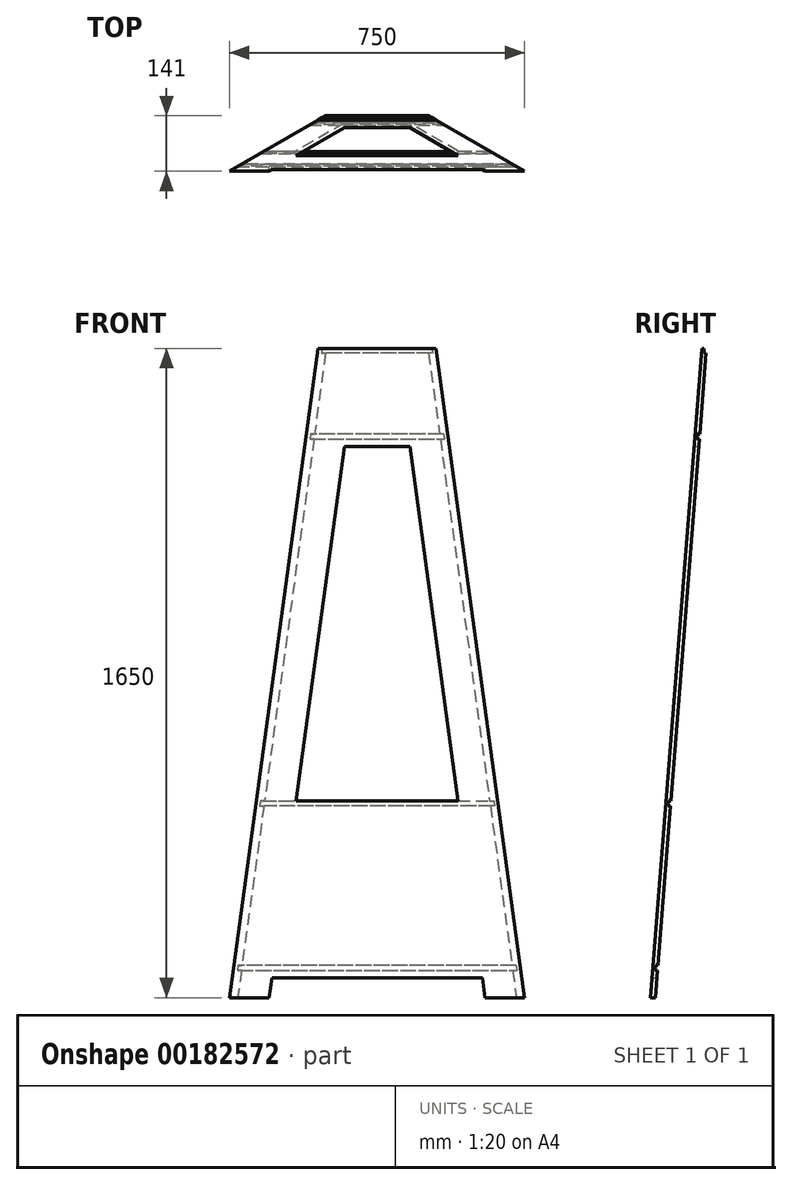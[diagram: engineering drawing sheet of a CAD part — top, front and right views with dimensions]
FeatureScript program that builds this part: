
annotation { "Feature Type Name" : "Feature", "Feature Type Description" : "" }
export const myFeature = defineFeature(function(context is Context, id is Id, definition is map)
    precondition{}
    {
        {
            var Q0;
            Q0=qCreatedBy(makeId("Front.planeOp"),FACE);
            var sketch = newSketch(context, id + "F0", { "sketchPlane" : qUnion([Q0])});
            skLineSegment(sketch, "E0", {"start": v(-375, 0) * mm, "end": v(375, 0) * mm});
            skLineSegment(sketch, "E1", {"start": v(0, 0) * mm, "end": v(0, 1650) * mm});
            skLineSegment(sketch, "E2", {"start": v(-150, 1650) * mm, "end": v(150, 1650) * mm});
            skSolve(sketch);
        }
        {
            var Q0;
            Q0=sQuery(id+"F0.wireOp",EDGE,"E2");
            cPoint(context, id + "F1", {"entities" : qUnion([Q0]), "parameter" : 0.5});
        }
        {
            var Q0;
            Q0=qCreatedBy(id+"F1",VERTEX);
            var Q1;
            Q1=sQuery(id+"F0.wireOp",EDGE,"E1");
            cPlane(context, id + "F2", {"entities" : qUnion([Q0, Q1]), "cplaneType" : CPlaneType.LINE_POINT, "offset" : 25 * mm, "width" : 150 * mm, "height" : 150 * mm});
        }
        {
            var Q0;
            Q0=qCreatedBy(makeId("Top.planeOp"),FACE);
            var sketch = newSketch(context, id + "F3", { "sketchPlane" : qUnion([Q0])});
            skCircle(sketch, "E3.cCircle", {"center": v(0, 0) * mm, "radius": 216.5 * mm, "construction": true});
            skLineSegment(sketch, "E3.0", {"start": v(375, -216.5) * mm, "end": v(-375, -216.5) * mm});
            skLineSegment(sketch, "E3.1", {"start": v(-375, -216.5) * mm, "end": v(0, 433.01) * mm});
            skLineSegment(sketch, "E3.2", {"start": v(0, 433.01) * mm, "end": v(375, -216.5) * mm});
            skPoint(sketch, "E3.0.midPoint", {"position": v(0, -216.5) * mm});
            skSolve(sketch);
        }
        {
            var Q0;
            Q0=qCreatedBy(id+"F2.planeOp",FACE);
            var sketch = newSketch(context, id + "F4", { "sketchPlane" : qUnion([Q0])});
            skCircle(sketch, "E4.cCircle", {"center": v(0, 0) * mm, "radius": 86.6 * mm, "construction": true});
            skLineSegment(sketch, "E4.0", {"start": v(150, -86.6) * mm, "end": v(-150, -86.6) * mm});
            skLineSegment(sketch, "E4.1", {"start": v(-150, -86.6) * mm, "end": v(0, 173.2) * mm});
            skLineSegment(sketch, "E4.2", {"start": v(0, 173.2) * mm, "end": v(150, -86.6) * mm});
            skPoint(sketch, "E4.0.midPoint", {"position": v(0, -86.6) * mm});
            skSolve(sketch);
        }
        {
            var Q0;
            Q0=makeQuery(id+"F3.imprint","IMPRINT",FACE,{"disambiguationData":[TD([[makeQuery(id+"F3.imprint","IMPRINT",EDGE,{"derivedFrom":sQuery(id+"F3.wireOp",EDGE,"E3.0")}),-1.0]])]});
            var Q1;
            Q1=makeQuery(id+"F4.imprint","IMPRINT",FACE,{"disambiguationData":[TD([[makeQuery(id+"F4.imprint","IMPRINT",EDGE,{"derivedFrom":sQuery(id+"F4.wireOp",EDGE,"E4.0")}),-1.0]])]});
            loft(context, id + "F5", {"sheetProfilesArray" : [{ "sheetProfileEntities" : qUnion([Q0]) }, { "sheetProfileEntities" : qUnion([Q1]) }]});
        }
        {
            var Q0;
            {var subQ0=sQuery(id+"F4.wireOp",EDGE,"E4.0");var subQ1=sQuery(id+"F4.wireOp",EDGE,"E4.1");var subQ2=sQuery(id+"F4.wireOp",EDGE,"E4.2");var subQ3=sQuery(id+"F3.wireOp",EDGE,"E3.0");var subQ4=sQuery(id+"F3.wireOp",EDGE,"E3.1");var subQ5=sQuery(id+"F3.wireOp",EDGE,"E3.2");Q0=makeQuery(id+"F5.opLoft","SWEPT_FACE",FACE,{"disambiguationData":[OSD([subQ3,subQ4,subQ5,subQ0,subQ1,subQ2]),TDD([makeQuery(id+"F3.imprint","INTERSECT",VERTEX,{"derivedFrom":[subQ3,subQ5]}),makeQuery(id+"F3.imprint","INTERSECT",VERTEX,{"derivedFrom":[subQ3,subQ4]}),makeQuery(id+"F3.imprint","IMPRINT",EDGE,{"derivedFrom":subQ3}),makeQuery(id+"F4.imprint","INTERSECT",VERTEX,{"derivedFrom":[subQ0,subQ2]}),makeQuery(id+"F4.imprint","INTERSECT",VERTEX,{"derivedFrom":[subQ0,subQ1]}),makeQuery(id+"F4.imprint","IMPRINT",EDGE,{"derivedFrom":subQ0})])]});}
            cPlane(context, id + "F6", {"entities" : qUnion([Q0]), "cplaneType" : CPlaneType.OFFSET, "offset" : 12 * mm, "oppositeDirection" : true, "width" : 150 * mm, "height" : 150 * mm});
        }
        {
            var Q0;
            Q0=qCreatedBy(id+"F6.planeOp",FACE);
            var sketch = newSketch(context, id + "F7", { "sketchPlane" : qUnion([Q0])});
            skCircle(sketch, "E5", {"center": v(0, 812.97) * mm, "radius": 960.24 * mm});
            skSolve(sketch);
        }
        {
            var Q0;
            Q0=qSketchRegion(id+"F7",true);
            extrude(context, id + "F8", {"entities" : qUnion([Q0]), "operationType" : NewBodyOperationType.REMOVE, "endBound" : BoundingType.THROUGH_ALL, "oppositeDirection" : true, "depth" : 25 * mm});
        }
        {
            var Q0;
            Q0=makeQuery(id+"F5.opLoft","CAP_FACE",FACE,{"disambiguationData":[OSD([makeQuery(id+"F4.imprint","IMPRINT",FACE,{"disambiguationData":[TD([[makeQuery(id+"F4.imprint","IMPRINT",EDGE,{"derivedFrom":sQuery(id+"F4.wireOp",EDGE,"E4.0")}),-1.0]])]})])],"isStart":true});
            var sketch = newSketch(context, id + "F9", { "sketchPlane" : qUnion([Q0])});
            skLineSegment(sketch, "E6", {"start": v(150, -86.6) * mm, "end": v(129.15, -74.57) * mm});
            skLineSegment(sketch, "E7", {"start": v(-150, -86.6) * mm, "end": v(-129.15, -74.57) * mm});
            skLineSegment(sketch, "E8", {"start": v(129.15, -74.57) * mm, "end": v(70, -40.41) * mm, "construction": true});
            skLineSegment(sketch, "E9", {"start": v(129.15, -74.57) * mm, "end": v(104.15, -31.26) * mm, "construction": true});
            skLineSegment(sketch, "E10", {"start": v(104.15, -31.26) * mm, "end": v(70, -40.41) * mm, "construction": true});
            skLineSegment(sketch, "E11.MirrorCS", {"start": v(79.15, -74.57) * mm, "end": v(70, -40.41) * mm, "construction": true});
            skLineSegment(sketch, "E12.MirrorCS", {"start": v(129.15, -74.57) * mm, "end": v(79.15, -74.57) * mm, "construction": true});
            skSolve(sketch);
        }
        {
            var Q0;
            Q0=makeQuery(id+"F5.opLoft","SWEPT_EDGE",EDGE,{"disambiguationData":[OSD([sQuery(id+"F3.wireOp",EDGE,"E3.0"),sQuery(id+"F3.wireOp",EDGE,"E3.1"),sQuery(id+"F4.wireOp",EDGE,"E4.0"),sQuery(id+"F4.wireOp",EDGE,"E4.1")])]});
            var Q1;
            Q1=sQuery(id+"F9.wireOp",EDGE,"E7");
            cPlane(context, id + "F10", {"entities" : qUnion([Q0, Q1]), "cplaneType" : CPlaneType.LINE_ANGLE, "offset" : 25 * mm, "angle" : 0 * degree, "width" : 150 * mm, "height" : 150 * mm});
        }
        {
            var Q0;
            Q0=makeQuery(id+"F5.opLoft","SWEPT_EDGE",EDGE,{"disambiguationData":[OSD([sQuery(id+"F3.wireOp",EDGE,"E3.0"),sQuery(id+"F3.wireOp",EDGE,"E3.2"),sQuery(id+"F4.wireOp",EDGE,"E4.0"),sQuery(id+"F4.wireOp",EDGE,"E4.2")])]});
            var Q1;
            Q1=sQuery(id+"F9.wireOp",EDGE,"E6");
            cPlane(context, id + "F11", {"entities" : qUnion([Q0, Q1]), "cplaneType" : CPlaneType.LINE_ANGLE, "offset" : 25 * mm, "angle" : 0 * degree, "width" : 150 * mm, "height" : 150 * mm});
        }
        {
            var Q0;
            Q0=qCreatedBy(id+"F11.planeOp",FACE);
            var sketch = newSketch(context, id + "F12", { "sketchPlane" : qUnion([Q0])});
            skCircle(sketch, "E13", {"center": v(304.07, 817.21) * mm, "radius": 870.23 * mm});
            skSolve(sketch);
        }
        {
            var Q0;
            Q0=qSketchRegion(id+"F12",true);
            extrude(context, id + "F13", {"entities" : qUnion([Q0]), "operationType" : NewBodyOperationType.REMOVE, "oppositeDirection" : true, "depth" : 25 * mm});
        }
        {
            var Q0;
            Q0=qCreatedBy(id+"F10.planeOp",FACE);
            var sketch = newSketch(context, id + "F14", { "sketchPlane" : qUnion([Q0])});
            skCircle(sketch, "E14", {"center": v(291.65, 811.12) * mm, "radius": 892.94 * mm});
            skSolve(sketch);
        }
        {
            var Q0;
            Q0=qSketchRegion(id+"F14",true);
            extrude(context, id + "F15", {"entities" : qUnion([Q0]), "operationType" : NewBodyOperationType.REMOVE, "depth" : 25 * mm});
        }
        {
            var Q0;
            Q0=qCreatedBy(makeId("Front.planeOp"),FACE);
            var sketch = newSketch(context, id + "F16", { "sketchPlane" : qUnion([Q0])});
            skLineSegment(sketch, "E15.0.0", {"start": v(-354.15, 0) * mm, "end": v(-129.15, 1650) * mm, "construction": true});
            skLineSegment(sketch, "E15.0.1", {"start": v(-129.15, 1650) * mm, "end": v(129.15, 1650) * mm});
            skLineSegment(sketch, "E15.0.2", {"start": v(129.15, 1650) * mm, "end": v(354.15, 0) * mm, "construction": true});
            skLineSegment(sketch, "E16.0.1", {"start": v(-150, 1650) * mm, "end": v(-375, 0) * mm, "construction": true});
            skLineSegment(sketch, "E16.0.3", {"start": v(375, 0) * mm, "end": v(150, 1650) * mm, "construction": true});
            skLineSegment(sketch, "E17", {"start": v(0, 0) * mm, "end": v(0, 50) * mm, "construction": true});
            skLineSegment(sketch, "E18", {"start": v(0, 1400) * mm, "end": v(0, 1650) * mm, "construction": true});
            skLineSegment(sketch, "E19", {"start": v(0, 1400) * mm, "end": v(0, 500) * mm, "construction": true});
            skLineSegment(sketch, "E20", {"start": v(0, 500) * mm, "end": v(0, 50) * mm, "construction": true});
            skLineSegment(sketch, "E21", {"start": v(205.9, 500) * mm, "end": v(-205.9, 500) * mm});
            skLineSegment(sketch, "E22", {"start": v(-205.9, 500) * mm, "end": v(-83.17, 1400) * mm});
            skLineSegment(sketch, "E23", {"start": v(-83.17, 1400) * mm, "end": v(83.17, 1400) * mm});
            skLineSegment(sketch, "E24", {"start": v(83.17, 1400) * mm, "end": v(205.9, 500) * mm});
            skLineSegment(sketch, "E25", {"start": v(-274.07, 0) * mm, "end": v(-267.26, 50) * mm});
            skLineSegment(sketch, "E26", {"start": v(-267.26, 50) * mm, "end": v(267.26, 50) * mm});
            skLineSegment(sketch, "E27", {"start": v(267.26, 50) * mm, "end": v(274.07, 0) * mm});
            skLineSegment(sketch, "E28", {"start": v(274.07, 0) * mm, "end": v(-274.07, 0) * mm});
            skSolve(sketch);
        }
        {
            var Q0;
            Q0=qCreatedBy(makeId("Front.planeOp"),FACE);
            var sketch = newSketch(context, id + "F17", { "sketchPlane" : qUnion([Q0])});
            skLineSegment(sketch, "E29.0", {"start": v(375, 0) * mm, "end": v(150, 1650) * mm, "construction": true});
            skLineSegment(sketch, "E30.0", {"start": v(129.15, 1650) * mm, "end": v(354.15, 0) * mm, "construction": true});
            skLineSegment(sketch, "E31.0", {"start": v(-354.15, 0) * mm, "end": v(-129.15, 1650) * mm, "construction": true});
            skLineSegment(sketch, "E32.0", {"start": v(-150, 1650) * mm, "end": v(-375, 0) * mm, "construction": true});
            skPoint(sketch, "E33.0", {"position": v(0, 50) * mm});
            skPoint(sketch, "E34.0", {"position": v(0, 500) * mm});
            skPoint(sketch, "E35.0", {"position": v(0, 1400) * mm});
            skLineSegment(sketch, "E36", {"start": v(181.36, 1420) * mm, "end": v(-181.36, 1420) * mm});
            skLineSegment(sketch, "E37", {"start": v(-181.36, 1420) * mm, "end": v(-179.73, 1432) * mm});
            skLineSegment(sketch, "E38", {"start": v(-179.73, 1432) * mm, "end": v(179.73, 1432) * mm});
            skLineSegment(sketch, "E39", {"start": v(181.36, 1420) * mm, "end": v(179.73, 1432) * mm});
            skLineSegment(sketch, "E40", {"start": v(150, 1650) * mm, "end": v(-150, 1650) * mm});
            skLineSegment(sketch, "E41", {"start": v(-150, 1650) * mm, "end": v(-151.64, 1638) * mm});
            skLineSegment(sketch, "E42", {"start": v(-151.64, 1638) * mm, "end": v(151.64, 1638) * mm});
            skLineSegment(sketch, "E43", {"start": v(306.82, 500) * mm, "end": v(-306.82, 500) * mm});
            skLineSegment(sketch, "E44", {"start": v(-306.82, 500) * mm, "end": v(-308.45, 488) * mm});
            skLineSegment(sketch, "E45", {"start": v(-308.45, 488) * mm, "end": v(308.45, 488) * mm});
            skLineSegment(sketch, "E46", {"start": v(306.82, 500) * mm, "end": v(308.45, 488) * mm});
            skLineSegment(sketch, "E47", {"start": v(365.45, 70) * mm, "end": v(-365.45, 70) * mm});
            skLineSegment(sketch, "E48", {"start": v(-365.45, 70) * mm, "end": v(-363.82, 82) * mm});
            skLineSegment(sketch, "E49", {"start": v(-363.82, 82) * mm, "end": v(363.82, 82) * mm});
            skLineSegment(sketch, "E50", {"start": v(363.82, 82) * mm, "end": v(365.45, 70) * mm});
            skLineSegment(sketch, "E51", {"start": v(150, 1650) * mm, "end": v(151.64, 1638) * mm});
            skSolve(sketch);
        }
        {
            var Q0;
            Q0=makeQuery(id+"F8.boolean.opBoolean","COPY",FACE,{"derivedFrom":makeQuery(id+"F8.opExtrude","CAP_FACE",FACE,{"disambiguationData":[OSD([sQuery(id+"F7.wireOp",EDGE,"E5")])],"isStart":true})});
            cPlane(context, id + "F18", {"entities" : qUnion([Q0]), "cplaneType" : CPlaneType.OFFSET, "offset" : 6 * mm, "oppositeDirection" : true, "width" : 150 * mm, "height" : 150 * mm});
        }
        {
            var Q0;
            Q0=qSketchRegion(id+"F17",true);
            var Q1;
            Q1=qCreatedBy(id+"F18.planeOp",FACE);
            extrude(context, id + "F19", {"entities" : qUnion([Q0]), "operationType" : NewBodyOperationType.REMOVE, "endBound" : BoundingType.UP_TO_SURFACE, "endBoundEntityFace" : qUnion([Q1]), "depth" : 25 * mm});
        }
        {
            var Q0;
            Q0=makeQuery(id+"F16.imprint","IMPRINT",FACE,{"disambiguationData":[TD([[makeQuery(id+"F16.imprint","IMPRINT",EDGE,{"derivedFrom":sQuery(id+"F16.wireOp",EDGE,"E25")}),-1.0]])]});
            var Q1;
            Q1=makeQuery(id+"F16.imprint","IMPRINT",FACE,{"disambiguationData":[TD([[makeQuery(id+"F16.imprint","IMPRINT",EDGE,{"derivedFrom":sQuery(id+"F16.wireOp",EDGE,"E21")}),-1.0]])]});
            extrude(context, id + "F20", {"entities" : qUnion([Q0, Q1]), "operationType" : NewBodyOperationType.REMOVE, "endBound" : BoundingType.THROUGH_ALL, "depth" : 25 * mm});
        }
    });
